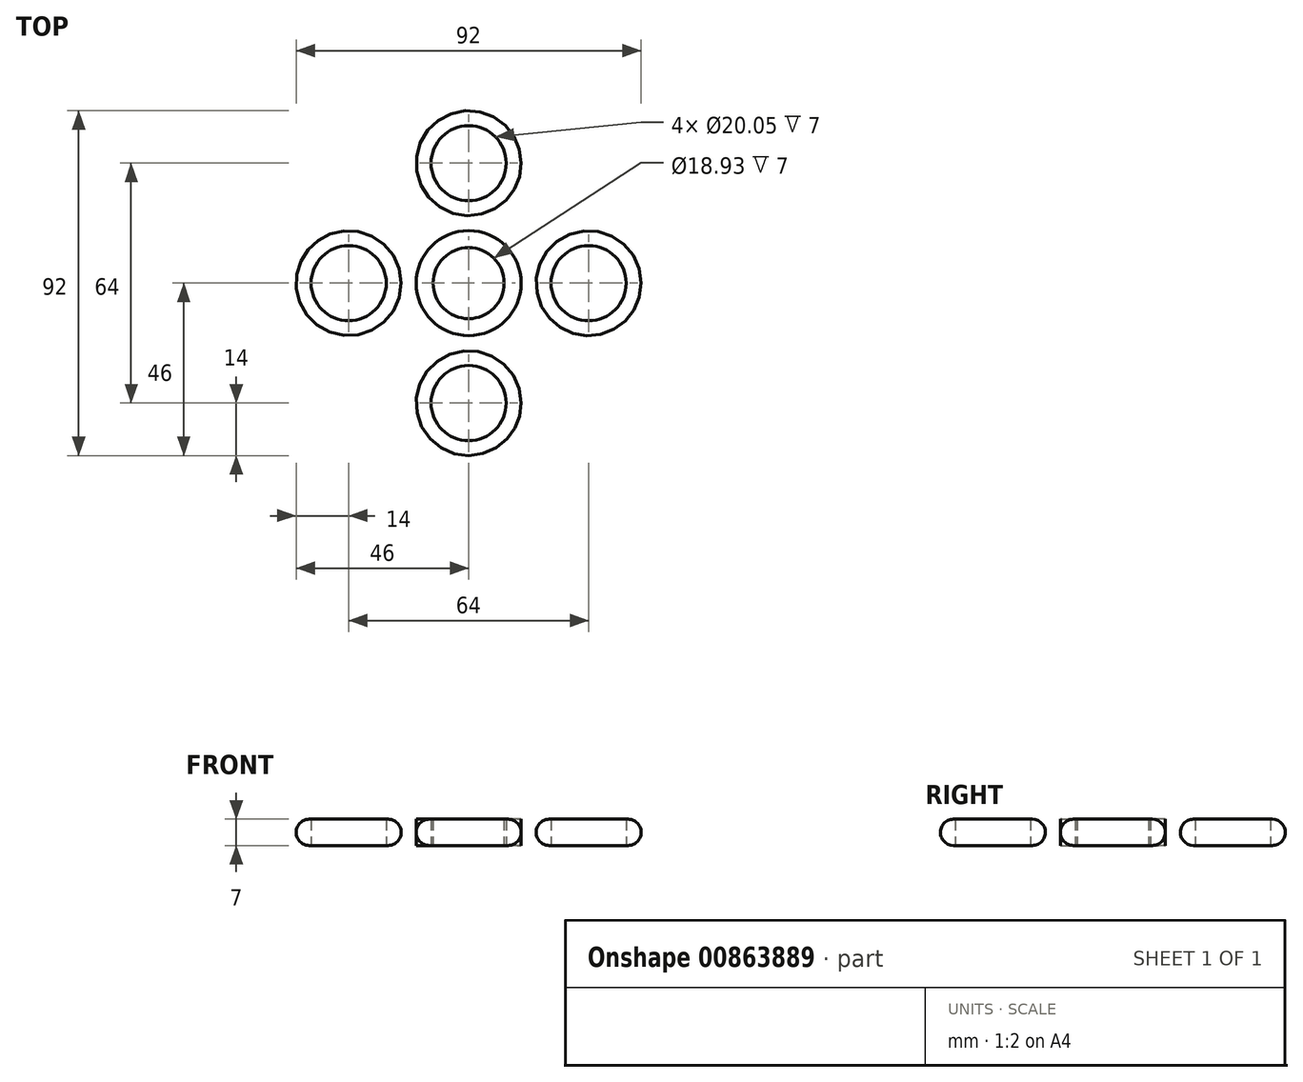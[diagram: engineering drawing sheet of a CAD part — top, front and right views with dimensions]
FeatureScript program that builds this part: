
annotation { "Feature Type Name" : "Feature", "Feature Type Description" : "" }
export const myFeature = defineFeature(function(context is Context, id is Id, definition is map)
    precondition{}
    {
        {
            var Q0;
            Q0=qCreatedBy(makeId("Top.planeOp"),FACE);
            var sketch = newSketch(context, id + "F0", { "sketchPlane" : qUnion([Q0])});
            skCircle(sketch, "E0", {"center": v(0, 32) * mm, "radius": 14 * mm});
            skCircle(sketch, "E1", {"center": v(0, 32) * mm, "radius": 10.03 * mm});
            skCircle(sketch, "E2", {"center": v(0, 0) * mm, "radius": 14 * mm});
            skCircle(sketch, "E3", {"center": v(0, 0) * mm, "radius": 9.47 * mm});
            skCircle(sketch, "E4.1.0", {"center": v(-32, 0) * mm, "radius": 14 * mm});
            skCircle(sketch, "E4.1.1", {"center": v(-32, 0) * mm, "radius": 10.03 * mm});
            skCircle(sketch, "E4.2.0", {"center": v(0, -32) * mm, "radius": 14 * mm});
            skCircle(sketch, "E4.2.1", {"center": v(0, -32) * mm, "radius": 10.03 * mm});
            skCircle(sketch, "E4.3.0", {"center": v(32, 0) * mm, "radius": 14 * mm});
            skCircle(sketch, "E4.3.1", {"center": v(32, 0) * mm, "radius": 10.03 * mm});
            skSolve(sketch);
        }
        {
            var Q0;
            Q0=qCreatedBy(makeId("Top.planeOp"),FACE);
            var sketch = newSketch(context, id + "F1", { "sketchPlane" : qUnion([Q0])});
            skLineSegment(sketch, "E5.bottom", {"start": v(-14, 32) * mm, "end": v(14, 32) * mm});
            skLineSegment(sketch, "E5.top", {"start": v(-14, 0) * mm, "end": v(14, 0) * mm});
            skLineSegment(sketch, "E5.left", {"start": v(-14, 32) * mm, "end": v(-14, 0) * mm});
            skLineSegment(sketch, "E5.right", {"start": v(14, 32) * mm, "end": v(14, 0) * mm});
            skLineSegment(sketch, "E6", {"start": v(0, 32) * mm, "end": v(0, 0) * mm});
            skLineSegment(sketch, "E7", {"start": v(-14, 16) * mm, "end": v(14, 16) * mm});
            skPoint(sketch, "E8", {"position": v(12, 16) * mm});
            skFitSpline(sketch, "E9", {"points": [v(14, 32) * mm, v(12, 16) * mm, v(14, 0) * mm], "startDerivative": vector(-6, -32) * mm, "endDerivative": vector(6, -32) * mm});
            skFitSpline(sketch, "E10.MirrorCS", {"points": [v(-14, 32) * mm, v(-12, 16) * mm, v(-14, 0) * mm], "startDerivative": vector(6, -32) * mm, "endDerivative": vector(-6, -32) * mm});
            skCircle(sketch, "E11", {"center": v(0, 32) * mm, "radius": 14 * mm});
            skCircle(sketch, "E12", {"center": v(0, 0) * mm, "radius": 14 * mm});
            skSolve(sketch);
        }
        {
            var Q0;
            Q0 = qSketchRegion(id + "F0", true);
            extrude(context, id + "F2", {"entities" : qUnion([Q0]), "depth" : 7 * mm, "offsetDistance" : 25 * mm});
        }
        {
            var Q0;
            {var subQ0=sQuery(id+"F1.wireOp",EDGE,"E11");var subQ1=sQuery(id+"F1.wireOp",EDGE,"E6");var subQ2=makeQuery(id+"F1.imprint","INTERSECT",VERTEX,{"derivedFrom":[subQ1,subQ0]});Q0=makeQuery(id+"F1.imprint","IMPRINT",FACE,{"disambiguationData":[TD([[makeQuery(id+"F1.imprint","IMPRINT",EDGE,{"disambiguationData":[TD([[subQ2,-1.0]])],"derivedFrom":subQ1}),-1.0]])]});}
            var Q1;
            {var subQ0=sQuery(id+"F1.wireOp",EDGE,"E7");var subQ1=sQuery(id+"F1.wireOp",EDGE,"E6");var subQ2=makeQuery(id+"F1.imprint","INTERSECT",VERTEX,{"derivedFrom":[subQ1,subQ0]});Q1=makeQuery(id+"F1.imprint","IMPRINT",FACE,{"disambiguationData":[TD([[makeQuery(id+"F1.imprint","IMPRINT",EDGE,{"disambiguationData":[TD([[subQ2,-1.0]])],"derivedFrom":subQ1}),-1.0]])]});}
            var Q2;
            {var subQ0=sQuery(id+"F1.wireOp",EDGE,"E11");var subQ1=sQuery(id+"F1.wireOp",EDGE,"E6");var subQ2=makeQuery(id+"F1.imprint","INTERSECT",VERTEX,{"derivedFrom":[subQ1,subQ0]});Q2=makeQuery(id+"F1.imprint","IMPRINT",FACE,{"disambiguationData":[TD([[makeQuery(id+"F1.imprint","IMPRINT",EDGE,{"disambiguationData":[TD([[subQ2,-1.0]])],"derivedFrom":subQ1}),1.0]])]});}
            var Q3;
            {var subQ0=sQuery(id+"F1.wireOp",EDGE,"E7");var subQ1=sQuery(id+"F1.wireOp",EDGE,"E6");var subQ2=makeQuery(id+"F1.imprint","INTERSECT",VERTEX,{"derivedFrom":[subQ1,subQ0]});Q3=makeQuery(id+"F1.imprint","IMPRINT",FACE,{"disambiguationData":[TD([[makeQuery(id+"F1.imprint","IMPRINT",EDGE,{"disambiguationData":[TD([[subQ2,-1.0]])],"derivedFrom":subQ1}),1.0]])]});}
            var Q4;
            {var subQ2=sQuery(id+"F1.wireOp",EDGE,"E5.bottom");var subQ4=sQuery(id+"F1.wireOp",EDGE,"E6");var subQ5=makeQuery(id+"F1.imprint","INTERSECT",VERTEX,{"derivedFrom":[subQ2,subQ4]});Q4=makeQuery(id+"F1.imprint","IMPRINT",FACE,{"disambiguationData":[TD([[makeQuery(id+"F1.imprint","IMPRINT",EDGE,{"disambiguationData":[TD([[subQ5,-1.0]])],"derivedFrom":subQ4}),1.0]])]});}
            var Q5;
            {var subQ2=sQuery(id+"F1.wireOp",EDGE,"E5.bottom");var subQ4=sQuery(id+"F1.wireOp",EDGE,"E6");var subQ5=makeQuery(id+"F1.imprint","INTERSECT",VERTEX,{"derivedFrom":[subQ2,subQ4]});Q5=makeQuery(id+"F1.imprint","IMPRINT",FACE,{"disambiguationData":[TD([[makeQuery(id+"F1.imprint","IMPRINT",EDGE,{"disambiguationData":[TD([[subQ5,-1.0]])],"derivedFrom":subQ4}),-1.0]])]});}
            extrude(context, id + "F3", {"entities" : qUnion([Q0, Q1, Q2, Q3, Q4, Q5]), "depth" : 7 * mm, "offsetDistance" : 25 * mm});
        }
        {
            var Q0;
            Q0=makeQuery(id+"F3.opExtrude","SWEPT_BODY",BODY,{"disambiguationData":[OSD([sQuery(id+"F1.wireOp",EDGE,"E9"),sQuery(id+"F1.wireOp",EDGE,"E10.MirrorCS"),sQuery(id+"F1.wireOp",EDGE,"E11"),sQuery(id+"F1.wireOp",EDGE,"E12")])]});
            var Q1;
            Q1=makeQuery(id+"F2.opExtrude","SWEPT_FACE",FACE,{"disambiguationData":[OSD([sQuery(id+"F0.wireOp",EDGE,"E2")])]});
            circularPattern(context, id + "F4", {"entities" : qUnion([Q0]), "axis" : qUnion([Q1]), "angle" : 360 * degree, "instanceCount" : 4, "equalSpace" : true});
        }
        {
            var Q0;
            Q0=makeQuery(id+"F2.opExtrude","CAP_EDGE",EDGE,{"disambiguationData":[OSD([sQuery(id+"F0.wireOp",EDGE,"E4.2.0")])],"isStart":false});
            var Q1;
            Q1=makeQuery(id+"F2.opExtrude","CAP_EDGE",EDGE,{"disambiguationData":[OSD([sQuery(id+"F0.wireOp",EDGE,"E4.2.0")])],"isStart":true});
            var Q2;
            Q2=makeQuery(id+"F2.opExtrude","CAP_EDGE",EDGE,{"disambiguationData":[OSD([sQuery(id+"F0.wireOp",EDGE,"E4.1.0")])],"isStart":true});
            var Q3;
            Q3=makeQuery(id+"F2.opExtrude","CAP_EDGE",EDGE,{"disambiguationData":[OSD([sQuery(id+"F0.wireOp",EDGE,"E4.1.0")])],"isStart":false});
            var Q4;
            Q4=makeQuery(id+"F2.opExtrude","CAP_EDGE",EDGE,{"disambiguationData":[OSD([sQuery(id+"F0.wireOp",EDGE,"E0")])],"isStart":false});
            var Q5;
            Q5=makeQuery(id+"F2.opExtrude","CAP_EDGE",EDGE,{"disambiguationData":[OSD([sQuery(id+"F0.wireOp",EDGE,"E0")])],"isStart":true});
            var Q6;
            Q6=makeQuery(id+"F2.opExtrude","CAP_EDGE",EDGE,{"disambiguationData":[OSD([sQuery(id+"F0.wireOp",EDGE,"E4.3.0")])],"isStart":false});
            var Q7;
            Q7=makeQuery(id+"F2.opExtrude","CAP_EDGE",EDGE,{"disambiguationData":[OSD([sQuery(id+"F0.wireOp",EDGE,"E4.3.0")])],"isStart":true});
            var Q8;
            Q8=makeQuery(id+"F4.opPattern","COPY",EDGE,{"derivedFrom":makeQuery(id+"F3.opExtrude","CAP_EDGE",EDGE,{"disambiguationData":[OSD([sQuery(id+"F1.wireOp",EDGE,"E9")])],"isStart":false}),"instanceName":"3"});
            var Q9;
            Q9=makeQuery(id+"F4.opPattern","COPY",EDGE,{"derivedFrom":makeQuery(id+"F3.opExtrude","CAP_EDGE",EDGE,{"disambiguationData":[OSD([sQuery(id+"F1.wireOp",EDGE,"E10.MirrorCS")])],"isStart":false}),"instanceName":"3"});
            var Q10;
            Q10=makeQuery(id+"F4.opPattern","COPY",EDGE,{"derivedFrom":makeQuery(id+"F3.opExtrude","CAP_EDGE",EDGE,{"disambiguationData":[OSD([sQuery(id+"F1.wireOp",EDGE,"E10.MirrorCS")])],"isStart":true}),"instanceName":"3"});
            var Q11;
            Q11=makeQuery(id+"F4.opPattern","COPY",EDGE,{"derivedFrom":makeQuery(id+"F3.opExtrude","CAP_EDGE",EDGE,{"disambiguationData":[OSD([sQuery(id+"F1.wireOp",EDGE,"E9")])],"isStart":true}),"instanceName":"3"});
            var Q12;
            Q12=makeQuery(id+"F4.opPattern","COPY",EDGE,{"derivedFrom":makeQuery(id+"F3.opExtrude","CAP_EDGE",EDGE,{"disambiguationData":[OSD([sQuery(id+"F1.wireOp",EDGE,"E10.MirrorCS")])],"isStart":false}),"instanceName":"1"});
            var Q13;
            Q13=makeQuery(id+"F4.opPattern","COPY",EDGE,{"derivedFrom":makeQuery(id+"F3.opExtrude","CAP_EDGE",EDGE,{"disambiguationData":[OSD([sQuery(id+"F1.wireOp",EDGE,"E10.MirrorCS")])],"isStart":true}),"instanceName":"1"});
            var Q14;
            Q14=makeQuery(id+"F4.opPattern","COPY",EDGE,{"derivedFrom":makeQuery(id+"F3.opExtrude","CAP_EDGE",EDGE,{"disambiguationData":[OSD([sQuery(id+"F1.wireOp",EDGE,"E9")])],"isStart":false}),"instanceName":"1"});
            var Q15;
            Q15=makeQuery(id+"F4.opPattern","COPY",EDGE,{"derivedFrom":makeQuery(id+"F3.opExtrude","CAP_EDGE",EDGE,{"disambiguationData":[OSD([sQuery(id+"F1.wireOp",EDGE,"E9")])],"isStart":true}),"instanceName":"1"});
            var Q16;
            Q16=makeQuery(id+"F4.opPattern","COPY",EDGE,{"derivedFrom":makeQuery(id+"F3.opExtrude","CAP_EDGE",EDGE,{"disambiguationData":[OSD([sQuery(id+"F1.wireOp",EDGE,"E10.MirrorCS")])],"isStart":false}),"instanceName":"2"});
            var Q17;
            Q17=makeQuery(id+"F4.opPattern","COPY",EDGE,{"derivedFrom":makeQuery(id+"F3.opExtrude","CAP_EDGE",EDGE,{"disambiguationData":[OSD([sQuery(id+"F1.wireOp",EDGE,"E10.MirrorCS")])],"isStart":true}),"instanceName":"2"});
            var Q18;
            Q18=makeQuery(id+"F4.opPattern","COPY",EDGE,{"derivedFrom":makeQuery(id+"F3.opExtrude","CAP_EDGE",EDGE,{"disambiguationData":[OSD([sQuery(id+"F1.wireOp",EDGE,"E9")])],"isStart":false}),"instanceName":"2"});
            var Q19;
            Q19=makeQuery(id+"F4.opPattern","COPY",EDGE,{"derivedFrom":makeQuery(id+"F3.opExtrude","CAP_EDGE",EDGE,{"disambiguationData":[OSD([sQuery(id+"F1.wireOp",EDGE,"E9")])],"isStart":true}),"instanceName":"2"});
            var Q20;
            Q20=makeQuery(id+"F3.opExtrude","CAP_EDGE",EDGE,{"disambiguationData":[OSD([sQuery(id+"F1.wireOp",EDGE,"E10.MirrorCS")])],"isStart":false});
            var Q21;
            Q21=makeQuery(id+"F3.opExtrude","CAP_EDGE",EDGE,{"disambiguationData":[OSD([sQuery(id+"F1.wireOp",EDGE,"E10.MirrorCS")])],"isStart":true});
            var Q22;
            Q22=makeQuery(id+"F3.opExtrude","CAP_EDGE",EDGE,{"disambiguationData":[OSD([sQuery(id+"F1.wireOp",EDGE,"E9")])],"isStart":false});
            var Q23;
            Q23=makeQuery(id+"F3.opExtrude","CAP_EDGE",EDGE,{"disambiguationData":[OSD([sQuery(id+"F1.wireOp",EDGE,"E9")])],"isStart":true});
            fillet(context, id + "F5", {"entities" : qUnion([Q0, Q1, Q2, Q3, Q4, Q5, Q6, Q7, Q8, Q9, Q10, Q11, Q12, Q13, Q14, Q15, Q16, Q17, Q18, Q19, Q20, Q21, Q22, Q23]), "radius" : 3.5 * mm, "tangentPropagation" : true, "allowEdgeOverflow" : false});
        }
        {
            var Q0;
            Q0=makeQuery(id+"F2.opExtrude","SWEPT_BODY",BODY,{"disambiguationData":[OSD([sQuery(id+"F0.wireOp",EDGE,"E4.1.0"),sQuery(id+"F0.wireOp",EDGE,"E4.1.1")])]});
            var Q1;
            Q1=makeQuery(id+"F2.opExtrude","SWEPT_BODY",BODY,{"disambiguationData":[OSD([sQuery(id+"F0.wireOp",EDGE,"E4.2.0"),sQuery(id+"F0.wireOp",EDGE,"E4.2.1")])]});
            var Q2;
            Q2=makeQuery(id+"F2.opExtrude","SWEPT_BODY",BODY,{"disambiguationData":[OSD([sQuery(id+"F0.wireOp",EDGE,"E4.3.0"),sQuery(id+"F0.wireOp",EDGE,"E4.3.1")])]});
            var Q3;
            Q3=makeQuery(id+"F2.opExtrude","SWEPT_BODY",BODY,{"disambiguationData":[OSD([sQuery(id+"F0.wireOp",EDGE,"E0"),sQuery(id+"F0.wireOp",EDGE,"E1")])]});
            var Q4;
            Q4=makeQuery(id+"F4.opPattern","COPY",BODY,{"derivedFrom":makeQuery(id+"F3.opExtrude","SWEPT_BODY",BODY,{"disambiguationData":[OSD([sQuery(id+"F1.wireOp",EDGE,"E5.bottom"),sQuery(id+"F1.wireOp",EDGE,"E9"),sQuery(id+"F1.wireOp",EDGE,"E10.MirrorCS"),sQuery(id+"F1.wireOp",EDGE,"E12")])]}),"instanceName":"3"});
            var Q5;
            Q5=makeQuery(id+"F3.opExtrude","SWEPT_BODY",BODY,{"disambiguationData":[OSD([sQuery(id+"F1.wireOp",EDGE,"E5.bottom"),sQuery(id+"F1.wireOp",EDGE,"E9"),sQuery(id+"F1.wireOp",EDGE,"E10.MirrorCS"),sQuery(id+"F1.wireOp",EDGE,"E12")])]});
            var Q6;
            Q6=makeQuery(id+"F4.opPattern","COPY",BODY,{"derivedFrom":makeQuery(id+"F3.opExtrude","SWEPT_BODY",BODY,{"disambiguationData":[OSD([sQuery(id+"F1.wireOp",EDGE,"E5.bottom"),sQuery(id+"F1.wireOp",EDGE,"E9"),sQuery(id+"F1.wireOp",EDGE,"E10.MirrorCS"),sQuery(id+"F1.wireOp",EDGE,"E12")])]}),"instanceName":"1"});
            var Q7;
            Q7=makeQuery(id+"F4.opPattern","COPY",BODY,{"derivedFrom":makeQuery(id+"F3.opExtrude","SWEPT_BODY",BODY,{"disambiguationData":[OSD([sQuery(id+"F1.wireOp",EDGE,"E5.bottom"),sQuery(id+"F1.wireOp",EDGE,"E9"),sQuery(id+"F1.wireOp",EDGE,"E10.MirrorCS"),sQuery(id+"F1.wireOp",EDGE,"E12")])]}),"instanceName":"2"});
            booleanBodies(context, id + "F6", {"operationType" : BooleanOperationType.SUBTRACTION, "tools" : qUnion([Q0, Q1, Q2, Q3]), "targets" : qUnion([Q4, Q5, Q6, Q7]), "keepTools" : true});
        }
        {
            var Q0;
            Q0=makeQuery(id+"F6.opBoolean","SPLIT",BODY,{"disambiguationData":[OD(1.0)],"derivedFrom":makeQuery(id+"F4.opPattern","COPY",BODY,{"derivedFrom":makeQuery(id+"F3.opExtrude","SWEPT_BODY",BODY,{"disambiguationData":[OSD([sQuery(id+"F1.wireOp",EDGE,"E5.bottom"),sQuery(id+"F1.wireOp",EDGE,"E9"),sQuery(id+"F1.wireOp",EDGE,"E10.MirrorCS"),sQuery(id+"F1.wireOp",EDGE,"E12")])]}),"instanceName":"3"})});
            var Q1;
            Q1=makeQuery(id+"F6.opBoolean","SPLIT",BODY,{"disambiguationData":[OD(1.0)],"derivedFrom":makeQuery(id+"F3.opExtrude","SWEPT_BODY",BODY,{"disambiguationData":[OSD([sQuery(id+"F1.wireOp",EDGE,"E5.bottom"),sQuery(id+"F1.wireOp",EDGE,"E9"),sQuery(id+"F1.wireOp",EDGE,"E10.MirrorCS"),sQuery(id+"F1.wireOp",EDGE,"E12")])]})});
            var Q2;
            Q2=makeQuery(id+"F6.opBoolean","SPLIT",BODY,{"disambiguationData":[OD(1.0)],"derivedFrom":makeQuery(id+"F4.opPattern","COPY",BODY,{"derivedFrom":makeQuery(id+"F3.opExtrude","SWEPT_BODY",BODY,{"disambiguationData":[OSD([sQuery(id+"F1.wireOp",EDGE,"E5.bottom"),sQuery(id+"F1.wireOp",EDGE,"E9"),sQuery(id+"F1.wireOp",EDGE,"E10.MirrorCS"),sQuery(id+"F1.wireOp",EDGE,"E12")])]}),"instanceName":"1"})});
            var Q3;
            Q3=makeQuery(id+"F6.opBoolean","SPLIT",BODY,{"disambiguationData":[OD(1.0)],"derivedFrom":makeQuery(id+"F4.opPattern","COPY",BODY,{"derivedFrom":makeQuery(id+"F3.opExtrude","SWEPT_BODY",BODY,{"disambiguationData":[OSD([sQuery(id+"F1.wireOp",EDGE,"E5.bottom"),sQuery(id+"F1.wireOp",EDGE,"E9"),sQuery(id+"F1.wireOp",EDGE,"E10.MirrorCS"),sQuery(id+"F1.wireOp",EDGE,"E12")])]}),"instanceName":"2"})});
            deleteBodies(context, id + "F7", {"entities" : qUnion([Q0, Q1, Q2, Q3])});
        }
    });
